# Revit family: Турникет RTD-20
name_source: partatom
category: Generic Models
units: mm (PartAtom-declared; Revit-internal decimal feet)

## family parameters
Always vertical = Yes
Can host rebar = No
Cut with Voids When Loaded = No
Part Type = Normal
Room Calculation Point = No
Round Connector Dimension = Use Diameter
Shared = No
Work Plane-Based = No

## types (4) — shared parameters
Current = 9 A
Dimensions = 1595х2480×2303 mm
Electrical connection = 220 V
IP Code = IP54
Manufacturer = PERCo
Number = 1
Operating temperature = from -40°C to +55°C
Passageway width = 630 mm
Rated power = 210 W
Throughput rate = 60 persons/min
Turnstile material = Steel painted RAL 5010
URL = https://www.perco.com
Unit of measurement = pcs
Voltage = 24 V
Weight = from 370 kg

## per-type parameters (varying)
| type | Full name | Material | Name | Rotor material |
| RTD-20.1 Motorized | RTD-20 Double Passage Full Height Rotor Turnstile | Housing and rotor ─ powder-coated galvanized steel | RTD-20 Double passage rotor turnstile | Steel, painted, white |
| RTD-20.1S Motorized | RTD-20S Double Passage Full Height Rotor Turnstile | Housing ─ powder-coated galvanized steel. Rotor ─ stainless steel | RTD-20S Double passage rotor turnstile | Steel, stainless AISI 304 |
| RTD-20.2 Electromechanical | RTD-20 Double Passage Full Height Rotor Turnstile | Housing and rotor ─ powder-coated galvanized steel | RTD-20 Double passage rotor turnstile | Steel, painted, white |
| RTD-20.2S Electromechanical | RTD-20S Double Passage Full Height Rotor Turnstile | Housing ─ powder-coated galvanized steel. Rotor ─ stainless steel | RTD-20S Double passage rotor turnstile | Steel, stainless AISI 304 |
